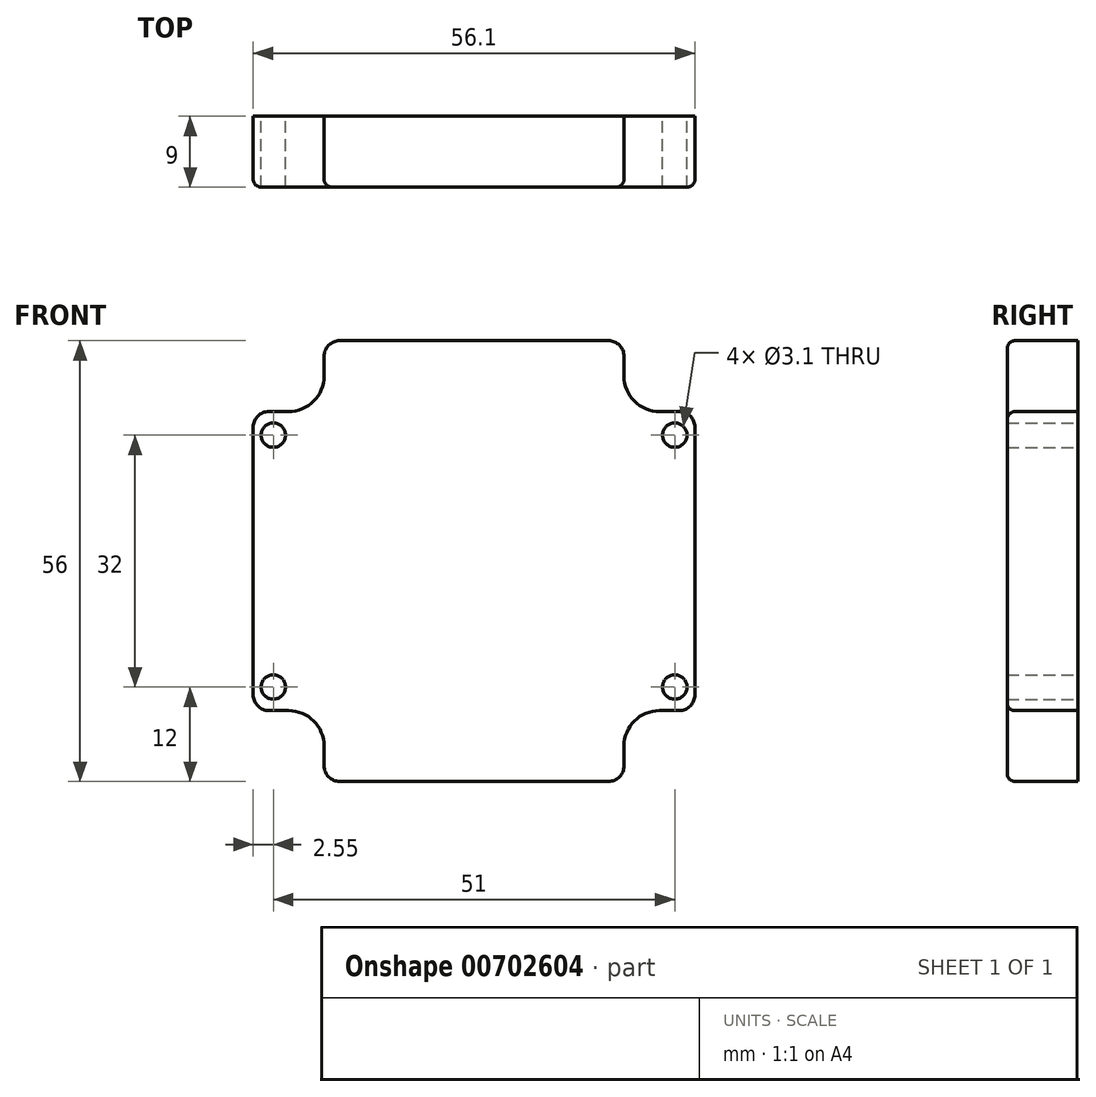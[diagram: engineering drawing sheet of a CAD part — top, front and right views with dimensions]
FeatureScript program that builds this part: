
annotation { "Feature Type Name" : "Feature", "Feature Type Description" : "" }
export const myFeature = defineFeature(function(context is Context, id is Id, definition is map)
    precondition{}
    {
        {
            var Q0;
            Q0=qCreatedBy(makeId("Front.planeOp"),FACE);
            var sketch = newSketch(context, id + "F0", { "sketchPlane" : qUnion([Q0])});
            skLineSegment(sketch, "E0.bottom", {"start": v(-17.05, 28) * mm, "end": v(17.05, 28) * mm});
            skLineSegment(sketch, "E0.top", {"start": v(-17.05, -28) * mm, "end": v(17.05, -28) * mm});
            skLineSegment(sketch, "E0.left", {"start": v(-28.05, 17) * mm, "end": v(-28.05, -17) * mm});
            skLineSegment(sketch, "E0.right", {"start": v(28.05, 17) * mm, "end": v(28.05, -17) * mm});
            skPoint(sketch, "E0.middle", {"position": v(0, 0) * mm});
            skCircle(sketch, "E1", {"center": v(-25.5, 16) * mm, "radius": 1.55 * mm});
            skCircle(sketch, "E2.MirrorC", {"center": v(25.5, 16) * mm, "radius": 1.55 * mm});
            skCircle(sketch, "E3.MirrorC", {"center": v(-25.5, -16) * mm, "radius": 1.55 * mm});
            skCircle(sketch, "E4.MirrorC", {"center": v(25.5, -16) * mm, "radius": 1.55 * mm});
            skArc(sketch, "E5", {"start": v(-23.55, 19) * mm, "mid": v(-20.37, 20.32) * mm, "end": v(-19.05, 23.5) * mm});
            skPoint(sketch, "E5.first.point", {"position": v(-28.05, 23.5) * mm});
            skPoint(sketch, "E5.second.point", {"position": v(-23.55, 28) * mm});
            skPoint(sketch, "E5.third.point", {"position": v(-19.64, 25.72) * mm});
            skLineSegment(sketch, "E6", {"start": v(-19.05, 23.5) * mm, "end": v(-19.05, 26) * mm});
            skLineSegment(sketch, "E7", {"start": v(-23.55, 19) * mm, "end": v(-26.05, 19) * mm});
            skPoint(sketch, "E8.orphan", {"position": v(-28.05, 28) * mm});
            skLineSegment(sketch, "E9.MirrorCS", {"start": v(23.55, 19) * mm, "end": v(26.05, 19) * mm});
            skLineSegment(sketch, "E10.MirrorCS", {"start": v(19.05, 23.5) * mm, "end": v(19.05, 26) * mm});
            skArc(sketch, "E11.MirrorCS", {"start": v(23.55, 19) * mm, "mid": v(20.37, 20.32) * mm, "end": v(19.05, 23.5) * mm});
            skLineSegment(sketch, "E12.MirrorCS", {"start": v(-23.55, -19) * mm, "end": v(-26.05, -19) * mm});
            skArc(sketch, "E13.MirrorCS", {"start": v(-23.55, -19) * mm, "mid": v(-20.37, -20.32) * mm, "end": v(-19.05, -23.5) * mm});
            skLineSegment(sketch, "E14.MirrorCS", {"start": v(-19.05, -23.5) * mm, "end": v(-19.05, -26) * mm});
            skLineSegment(sketch, "E15.MirrorCS", {"start": v(19.05, -23.5) * mm, "end": v(19.05, -26) * mm});
            skArc(sketch, "E16.MirrorCS", {"start": v(23.55, -19) * mm, "mid": v(20.37, -20.32) * mm, "end": v(19.05, -23.5) * mm});
            skLineSegment(sketch, "E17.MirrorCS", {"start": v(23.55, -19) * mm, "end": v(26.05, -19) * mm});
            skPoint(sketch, "E18.orphan", {"position": v(-28.05, -28) * mm});
            skPoint(sketch, "E19.orphan", {"position": v(28.05, -28) * mm});
            skPoint(sketch, "E20.orphan", {"position": v(28.05, 28) * mm});
            skPoint(sketch, "E21.visualSharp", {"position": v(-19.05, 28) * mm});
            skArc(sketch, "E21.filletArc", {"start": v(-17.05, 28) * mm, "mid": v(-18.46, 27.41) * mm, "end": v(-19.05, 26) * mm});
            skPoint(sketch, "E22.visualSharp", {"position": v(19.05, 28) * mm});
            skArc(sketch, "E22.filletArc", {"start": v(19.05, 26) * mm, "mid": v(18.46, 27.41) * mm, "end": v(17.05, 28) * mm});
            skPoint(sketch, "E23.visualSharp", {"position": v(28.05, 19) * mm});
            skArc(sketch, "E23.filletArc", {"start": v(28.05, 17) * mm, "mid": v(27.46, 18.41) * mm, "end": v(26.05, 19) * mm});
            skPoint(sketch, "E24.visualSharp", {"position": v(-28.05, 19) * mm});
            skArc(sketch, "E24.filletArc", {"start": v(-26.05, 19) * mm, "mid": v(-27.46, 18.41) * mm, "end": v(-28.05, 17) * mm});
            skPoint(sketch, "E25.visualSharp", {"position": v(-28.05, -19) * mm});
            skArc(sketch, "E25.filletArc", {"start": v(-28.05, -17) * mm, "mid": v(-27.46, -18.41) * mm, "end": v(-26.05, -19) * mm});
            skPoint(sketch, "E26.visualSharp", {"position": v(-19.05, -28) * mm});
            skArc(sketch, "E26.filletArc", {"start": v(-19.05, -26) * mm, "mid": v(-18.46, -27.41) * mm, "end": v(-17.05, -28) * mm});
            skPoint(sketch, "E27.visualSharp", {"position": v(19.05, -28) * mm});
            skArc(sketch, "E27.filletArc", {"start": v(17.05, -28) * mm, "mid": v(18.46, -27.41) * mm, "end": v(19.05, -26) * mm});
            skPoint(sketch, "E28.visualSharp", {"position": v(28.05, -19) * mm});
            skArc(sketch, "E28.filletArc", {"start": v(26.05, -19) * mm, "mid": v(27.46, -18.41) * mm, "end": v(28.05, -17) * mm});
            skSolve(sketch);
        }
        {
            var Q0;
            Q0=makeQuery(id+"F0.imprint","IMPRINT",FACE,{"disambiguationData":[TD([[makeQuery(id+"F0.imprint","IMPRINT",EDGE,{"derivedFrom":sQuery(id+"F0.wireOp",EDGE,"E0.bottom")}),-1.0]])]});
            extrude(context, id + "F1", {"entities" : qUnion([Q0]), "depth" : 9 * mm, "offsetDistance" : 25 * mm});
        }
        {
            var Q0;
            Q0=makeQuery(id+"F1.opExtrude","CAP_EDGE",EDGE,{"disambiguationData":[OSD([sQuery(id+"F0.wireOp",EDGE,"E24.filletArc")])],"isStart":false});
            fillet(context, id + "F2", {"entities" : qUnion([Q0]), "radius" : 1 * mm, "tangentPropagation" : true, "allowEdgeOverflow" : false});
        }
    });
